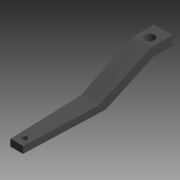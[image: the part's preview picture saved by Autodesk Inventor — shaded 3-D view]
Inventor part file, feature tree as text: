
AUTODESK INVENTOR PART (.ipt)
format: ipt  version: 2015 (Build 190159000, 159)  size: 81,408 bytes
history: native  units: mm (DEFAULTED — no unit token found)
features: chamfer x2, hole x2, extrude x1, sketch x1
ambient origin geometry x8: Origin, YZ Plane, XZ Plane, XY Plane, X Axis, Y Axis, Z Axis, Center Point
bodies: Solid1 (feature_tree)
feature tree (6):
  extrude  "Extrusion1"  Depth=173.99224mm
  chamfer  "Chamfer1"  Distance=25.0mm
  chamfer  "Chamfer2"  Distance=37.0mm
  hole  "Hole1"  [1 undecoded]
  hole  "Hole2"  [1 undecoded]
  sketch  "Sketch1"  dims[d0=8.0mm d1=173.99224mm d2=25.0mm d3=37.0mm d4=11.0mm d5=27.052603mm d6=22.0mm d7=0.0mm d8=100.0mm d9=3.5mm d10=45.0deg d11=100.0mm d12=3.5mm d13=45.0deg d14=9.0mm d15=11.0mm d16=6.0mm d17=6.0mm d18=4.0mm d19=2.0mm d20=90.0deg d21=8.0mm d22=20.594885mm d23=16.0mm d24=11.0mm d25=11.0mm d26=6.0mm d27=4.0mm d28=2.0mm d29=90.0deg d30=8.0mm d31=20.594885mm]
note: 2 required parameter values undecoded (feature->parameter linkage not recoverable at this tier; creation-order binding heuristic only, values carry confidence <= 0.55)
